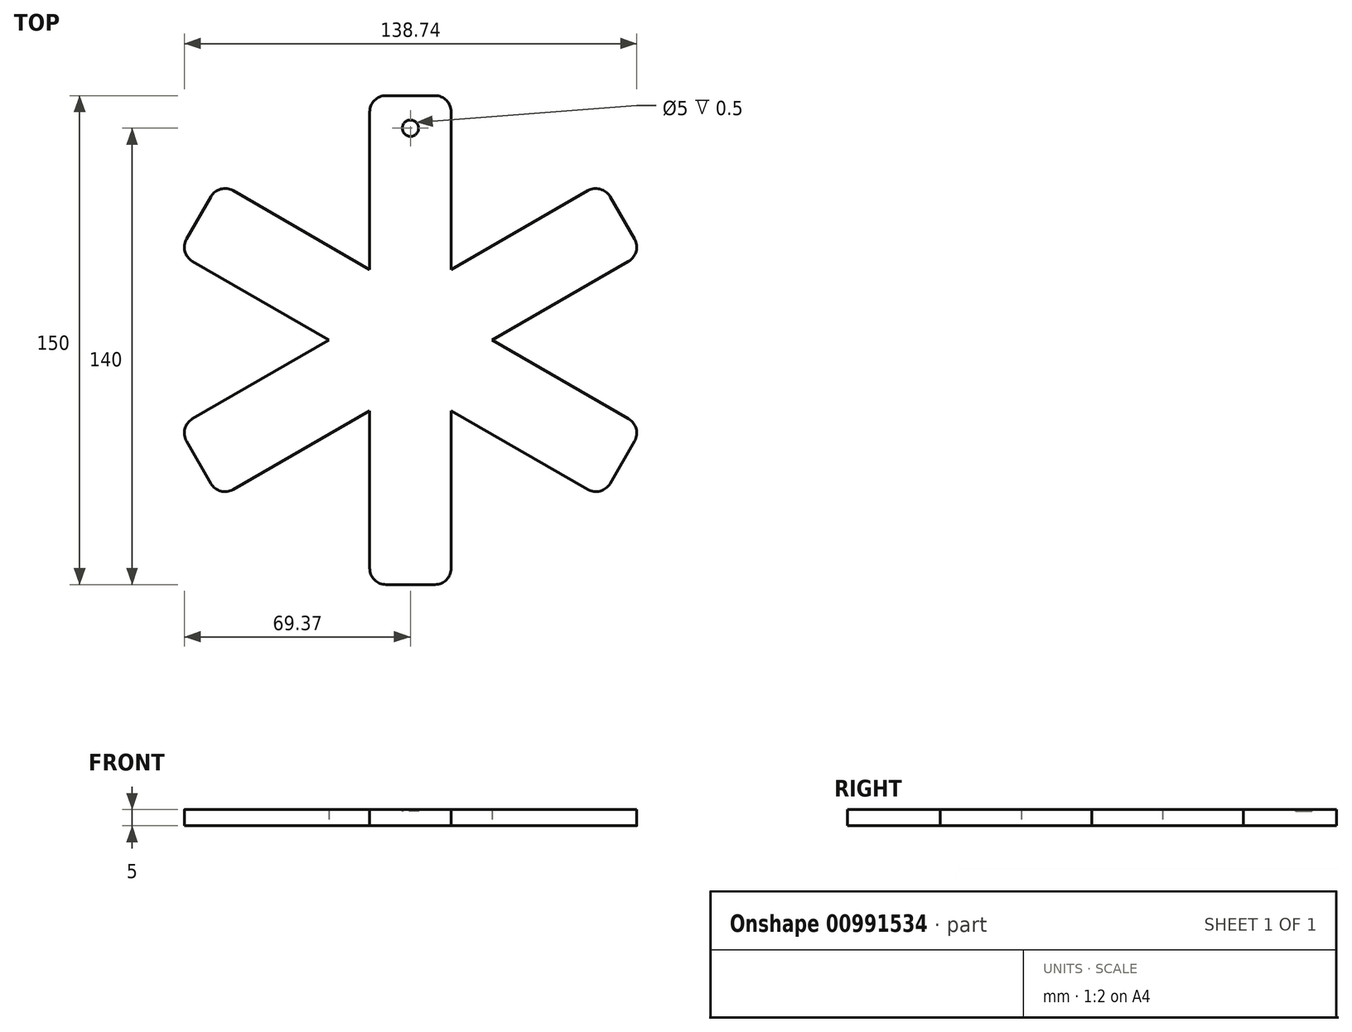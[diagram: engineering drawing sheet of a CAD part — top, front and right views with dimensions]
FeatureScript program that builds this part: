
annotation { "Feature Type Name" : "Feature", "Feature Type Description" : "" }
export const myFeature = defineFeature(function(context is Context, id is Id, definition is map)
    precondition{}
    {
        {
            var Q0;
            Q0=qCreatedBy(makeId("Top.planeOp"),FACE);
            var sketch = newSketch(context, id + "F0", { "sketchPlane" : qUnion([Q0])});
            skLineSegment(sketch, "E0.bottom", {"start": v(-12.5, 75) * mm, "end": v(12.5, 75) * mm});
            skLineSegment(sketch, "E0.top", {"start": v(-12.5, -75) * mm, "end": v(12.5, -75) * mm});
            skLineSegment(sketch, "E0.left", {"start": v(-12.5, 75) * mm, "end": v(-12.5, 21.65) * mm});
            skLineSegment(sketch, "E0.right", {"start": v(12.5, 75) * mm, "end": v(12.5, 21.65) * mm});
            skPoint(sketch, "E0.middle", {"position": v(0, 0) * mm});
            skLineSegment(sketch, "E1.1.1", {"start": v(-58.7, -48.33) * mm, "end": v(-71.2, -26.67) * mm});
            skLineSegment(sketch, "E1.1.2", {"start": v(-71.2, -26.67) * mm, "end": v(-25, 0) * mm});
            skLineSegment(sketch, "E1.1.3", {"start": v(-58.7, -48.33) * mm, "end": v(-12.5, -21.65) * mm});
            skLineSegment(sketch, "E1.1.4", {"start": v(71.2, 26.67) * mm, "end": v(58.7, 48.33) * mm});
            skLineSegment(sketch, "E1.2.1", {"start": v(71.2, -26.67) * mm, "end": v(58.7, -48.33) * mm});
            skLineSegment(sketch, "E1.2.2", {"start": v(58.7, -48.33) * mm, "end": v(12.5, -21.65) * mm});
            skLineSegment(sketch, "E1.2.3", {"start": v(71.2, -26.67) * mm, "end": v(25, 0) * mm});
            skLineSegment(sketch, "E1.2.4", {"start": v(-58.7, 48.33) * mm, "end": v(-71.2, 26.67) * mm});
            skLineSegment(sketch, "E2", {"start": v(-12.5, -21.65) * mm, "end": v(-12.5, -75) * mm});
            skLineSegment(sketch, "E3", {"start": v(12.5, -21.65) * mm, "end": v(12.5, -75) * mm});
            skLineSegment(sketch, "E4", {"start": v(-12.5, 21.65) * mm, "end": v(-58.7, 48.33) * mm});
            skLineSegment(sketch, "E5", {"start": v(12.5, 21.65) * mm, "end": v(58.7, 48.33) * mm});
            skLineSegment(sketch, "E6.trimOffspring", {"start": v(-25, 0) * mm, "end": v(-71.2, 26.67) * mm});
            skLineSegment(sketch, "E7.trimOffspring", {"start": v(25, 0) * mm, "end": v(71.2, 26.67) * mm});
            skSolve(sketch);
        }
        {
            var Q0;
            Q0 = qSketchRegion(id + "F0", true);
            extrude(context, id + "F1", {"entities" : qUnion([Q0]), "depth" : 5 * mm, "offsetDistance" : 25 * mm});
        }
        {
            var Q0;
            Q0=makeQuery(id+"F1.opExtrude","SWEPT_EDGE",EDGE,{"disambiguationData":[OSD([sQuery(id+"F0.wireOp",EDGE,"E1.1.1"),sQuery(id+"F0.wireOp",EDGE,"E1.1.2")])]});
            var Q1;
            Q1=makeQuery(id+"F1.opExtrude","SWEPT_EDGE",EDGE,{"disambiguationData":[OSD([sQuery(id+"F0.wireOp",EDGE,"E1.1.1"),sQuery(id+"F0.wireOp",EDGE,"E1.1.3")])]});
            var Q2;
            Q2=makeQuery(id+"F1.opExtrude","SWEPT_EDGE",EDGE,{"disambiguationData":[OSD([sQuery(id+"F0.wireOp",EDGE,"E0.top"),sQuery(id+"F0.wireOp",EDGE,"E2")])]});
            var Q3;
            Q3=makeQuery(id+"F1.opExtrude","SWEPT_EDGE",EDGE,{"disambiguationData":[OSD([sQuery(id+"F0.wireOp",EDGE,"E0.top"),sQuery(id+"F0.wireOp",EDGE,"E3")])]});
            var Q4;
            Q4=makeQuery(id+"F1.opExtrude","SWEPT_EDGE",EDGE,{"disambiguationData":[OSD([sQuery(id+"F0.wireOp",EDGE,"E1.2.4"),sQuery(id+"F0.wireOp",EDGE,"E6.trimOffspring")])]});
            var Q5;
            Q5=makeQuery(id+"F1.opExtrude","SWEPT_EDGE",EDGE,{"disambiguationData":[OSD([sQuery(id+"F0.wireOp",EDGE,"E1.2.1"),sQuery(id+"F0.wireOp",EDGE,"E1.2.2")])]});
            var Q6;
            Q6=makeQuery(id+"F1.opExtrude","SWEPT_EDGE",EDGE,{"disambiguationData":[OSD([sQuery(id+"F0.wireOp",EDGE,"E1.2.1"),sQuery(id+"F0.wireOp",EDGE,"E1.2.3")])]});
            var Q7;
            Q7=makeQuery(id+"F1.opExtrude","SWEPT_EDGE",EDGE,{"disambiguationData":[OSD([sQuery(id+"F0.wireOp",EDGE,"E1.1.4"),sQuery(id+"F0.wireOp",EDGE,"E7.trimOffspring")])]});
            var Q8;
            Q8=makeQuery(id+"F1.opExtrude","SWEPT_EDGE",EDGE,{"disambiguationData":[OSD([sQuery(id+"F0.wireOp",EDGE,"E1.1.4"),sQuery(id+"F0.wireOp",EDGE,"E5")])]});
            var Q9;
            Q9=makeQuery(id+"F1.opExtrude","SWEPT_EDGE",EDGE,{"disambiguationData":[OSD([sQuery(id+"F0.wireOp",EDGE,"E0.bottom"),sQuery(id+"F0.wireOp",EDGE,"E0.right")])]});
            var Q10;
            Q10=makeQuery(id+"F1.opExtrude","SWEPT_EDGE",EDGE,{"disambiguationData":[OSD([sQuery(id+"F0.wireOp",EDGE,"E0.bottom"),sQuery(id+"F0.wireOp",EDGE,"E0.left")])]});
            var Q11;
            Q11=makeQuery(id+"F1.opExtrude","SWEPT_EDGE",EDGE,{"disambiguationData":[OSD([sQuery(id+"F0.wireOp",EDGE,"E1.2.4"),sQuery(id+"F0.wireOp",EDGE,"E4")])]});
            fillet(context, id + "F2", {"entities" : qUnion([Q0, Q1, Q2, Q3, Q4, Q5, Q6, Q7, Q8, Q9, Q10, Q11]), "radius" : 5 * mm, "tangentPropagation" : true, "allowEdgeOverflow" : false});
        }
        {
            var Q0;
            Q0=makeQuery(id+"F1.opExtrude","CAP_FACE",FACE,{"disambiguationData":[OSD([sQuery(id+"F0.wireOp",EDGE,"E0.bottom"),sQuery(id+"F0.wireOp",EDGE,"E0.top"),sQuery(id+"F0.wireOp",EDGE,"E0.left"),sQuery(id+"F0.wireOp",EDGE,"E0.right"),sQuery(id+"F0.wireOp",EDGE,"E1.1.1"),sQuery(id+"F0.wireOp",EDGE,"E1.1.2"),sQuery(id+"F0.wireOp",EDGE,"E1.1.3"),sQuery(id+"F0.wireOp",EDGE,"E1.1.4"),sQuery(id+"F0.wireOp",EDGE,"E1.2.1"),sQuery(id+"F0.wireOp",EDGE,"E1.2.2"),sQuery(id+"F0.wireOp",EDGE,"E1.2.3"),sQuery(id+"F0.wireOp",EDGE,"E1.2.4"),sQuery(id+"F0.wireOp",EDGE,"E2"),sQuery(id+"F0.wireOp",EDGE,"E3"),sQuery(id+"F0.wireOp",EDGE,"E4"),sQuery(id+"F0.wireOp",EDGE,"E5"),sQuery(id+"F0.wireOp",EDGE,"E6.trimOffspring"),sQuery(id+"F0.wireOp",EDGE,"E7.trimOffspring")])],"isStart":false});
            var sketch = newSketch(context, id + "F3", { "sketchPlane" : qUnion([Q0])});
            skCircle(sketch, "E8", {"center": v(0, 65) * mm, "radius": 2.5 * mm});
            skSolve(sketch);
        }
        {
            var Q0;
            Q0 = qSketchRegion(id + "F3", true);
            extrude(context, id + "F4", {"entities" : qUnion([Q0]), "operationType" : NewBodyOperationType.REMOVE, "oppositeDirection" : true, "depth" : 0.5 * mm, "offsetDistance" : 25 * mm});
        }
    });
